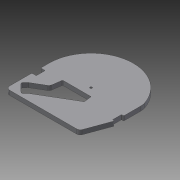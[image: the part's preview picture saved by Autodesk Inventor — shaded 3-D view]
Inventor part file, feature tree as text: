
AUTODESK INVENTOR PART (.ipt)
format: ipt  version: 2015 (Build 190159000, 159)  size: 214,528 bytes
history: native  units: mm
features: fillet x6, extrude x4, sketch x4, chamfer x2, projected_geometry x1
ambient origin geometry x8: Origin, YZ Plane, XZ Plane, XY Plane, X Axis, Y Axis, Z Axis, Center Point
bodies: Solid1 (feature_tree)
feature tree (17):
  extrude  "Extrusion1"  Depth=57.0mm
  fillet  "Fillet1"  Radius=20.0mm
  fillet  "Fillet2"  Radius=6.0mm
  fillet  "Fillet3"  Radius=12.0mm
  extrude  "Extrusion2"  Depth=3.0mm
  chamfer  "Chamfer1"  Distance=47.0mm
  chamfer  "Chamfer2"  Distance=58.0mm
  fillet  "Fillet4"  Radius=6.0mm
  extrude  "Extrusion3"  Depth=0.5mm
  fillet  "Fillet5"  Radius=1.0mm
  extrude  "Extrusion4"  Depth=5.0mm
  fillet  "Fillet6"  Radius=41.5mm
  sketch  "Sketch1"  dims[d0=3.0mm d1=57.0mm d2=20.0mm d3=6.0mm d4=12.0mm]
  sketch  "Sketch2"  dims[d5=55.0mm d6=3.0mm]
  sketch  "Sketch3"  dims[d7=19.198622mm]
  sketch  "Sketch4"  dims[d8=99.0mm d9=47.0mm d10=58.0mm d11=6.0mm d12=0.0mm d13=0.5mm d14=1.0mm d15=5.0mm d16=41.5mm d17=11.0mm d18=9.0mm d19=12.0mm d20=1.5mm d21=0.0mm d22=11.0mm d23=1.5mm d24=45.0deg d25=11.0mm d26=1.5mm d27=45.0deg d28=1.0mm d29=103.0mm d30=18.0mm d31=9.0mm d32=58.0mm d33=1.5mm d34=0.0mm d35=2.0mm d36=10.0mm d37=0.0mm d38=5.0mm]
  projected_geometry  "Projected Loop1"
